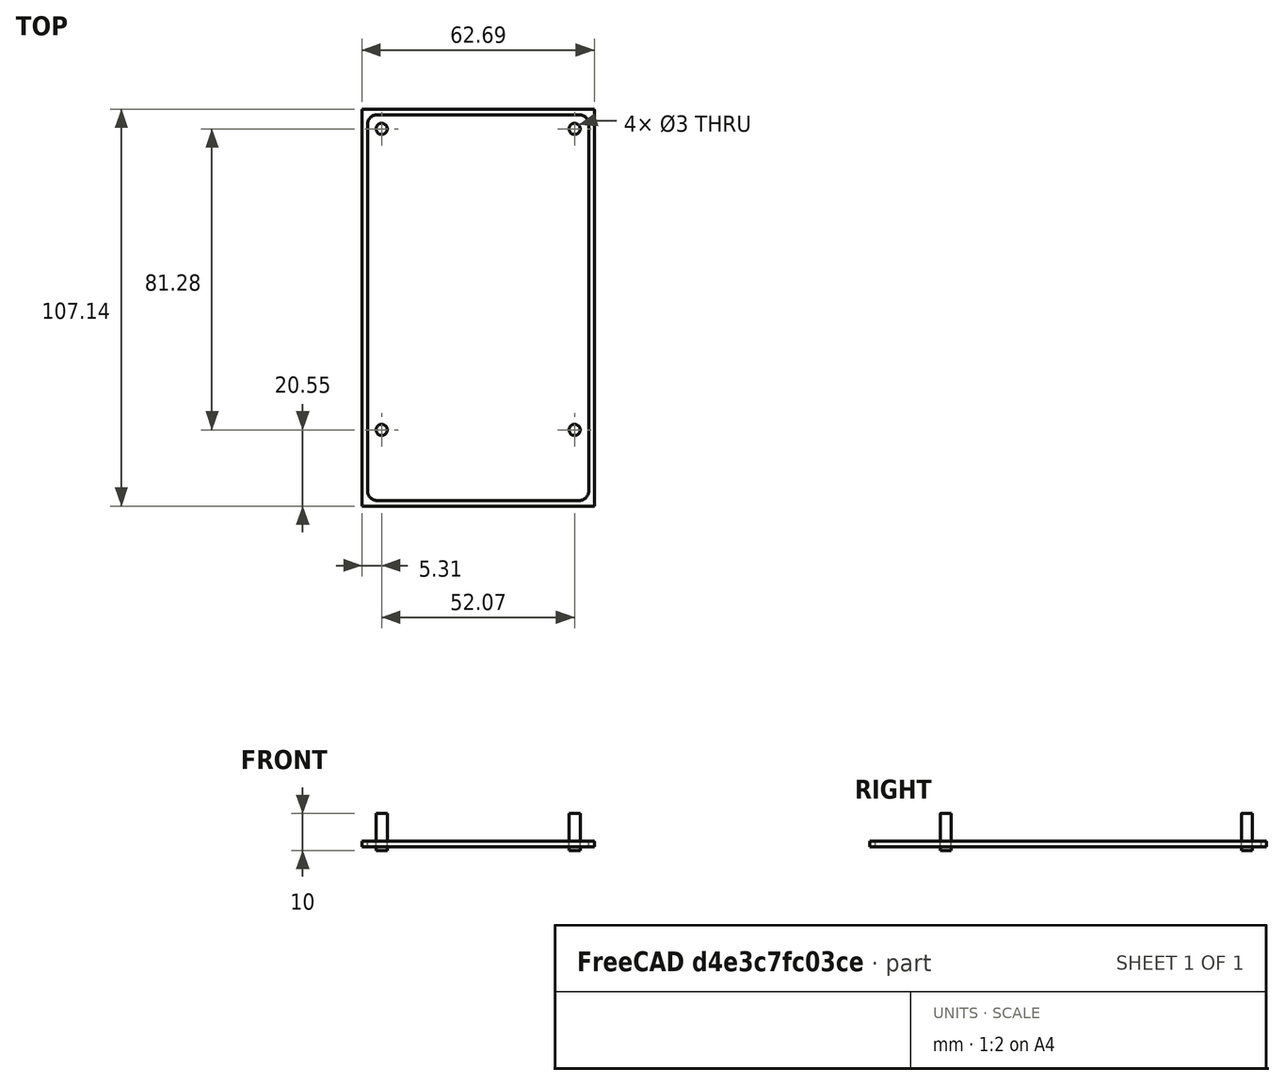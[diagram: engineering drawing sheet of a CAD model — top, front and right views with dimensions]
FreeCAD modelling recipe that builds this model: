
FCSTD DOCUMENT  (FreeCAD 1.0R39109 (Git))
Label: MacroPad-Case
License: All rights reserved
LicenseURL: https://en.wikipedia.org/wiki/All_rights_reserved
objects: Part::Cylinder×4, Part::Feature×1, Part::Box×1, App::DocumentObjectGroup×1
note: 6 computed .brp shape members not serialized (recipe doc carries the construction recipe); baked Part::Feature solids carry a one-line shape summary decoded from their .brp

FEATURE [Part::Feature] Part__Feature  label="Board"
  shape: bbox 59.69 x 104.1 x 1.57 mm, 14 faces (baked)
FEATURE [Part::Box] Box  label="Cube"
  AttacherType = Attacher::AttachEngine3D
  Height = 1.57
  Length = 62.69
  Placement = pos=(-1.5,-1.5,0) rot=(0,0,1;0rad)
  Width = 107.14
FEATURE [Part::Cylinder] Cylinder
  Angle = 360
  AttacherType = Attacher::AttachEngine3D
  FirstAngle = 0
  Height = 10
  Placement = pos=(3.81,19.05,-1) rot=(0,0,1;0rad)
  Radius = 1.5
  SecondAngle = 0
FEATURE [Part::Cylinder] Cylinder001
  Angle = 360
  AttacherType = Attacher::AttachEngine3D
  FirstAngle = 0
  Height = 10
  Placement = pos=(55.88,19.05,-1) rot=(0,0,1;0rad)
  Radius = 1.5
  SecondAngle = 0
FEATURE [Part::Cylinder] Cylinder002
  Angle = 360
  AttacherType = Attacher::AttachEngine3D
  FirstAngle = 0
  Height = 10
  Placement = pos=(3.81,100.33,-1) rot=(0,0,1;0rad)
  Radius = 1.5
  SecondAngle = 0
FEATURE [Part::Cylinder] Cylinder003
  Angle = 360
  AttacherType = Attacher::AttachEngine3D
  FirstAngle = 0
  Height = 10
  Placement = pos=(55.88,100.33,-1) rot=(0,0,1;0rad)
  Radius = 1.5
  SecondAngle = 0
FEATURE [App::DocumentObjectGroup] Group  label="Posts"
  Group = -> [Cylinder,Cylinder001,Cylinder002,Cylinder003]
